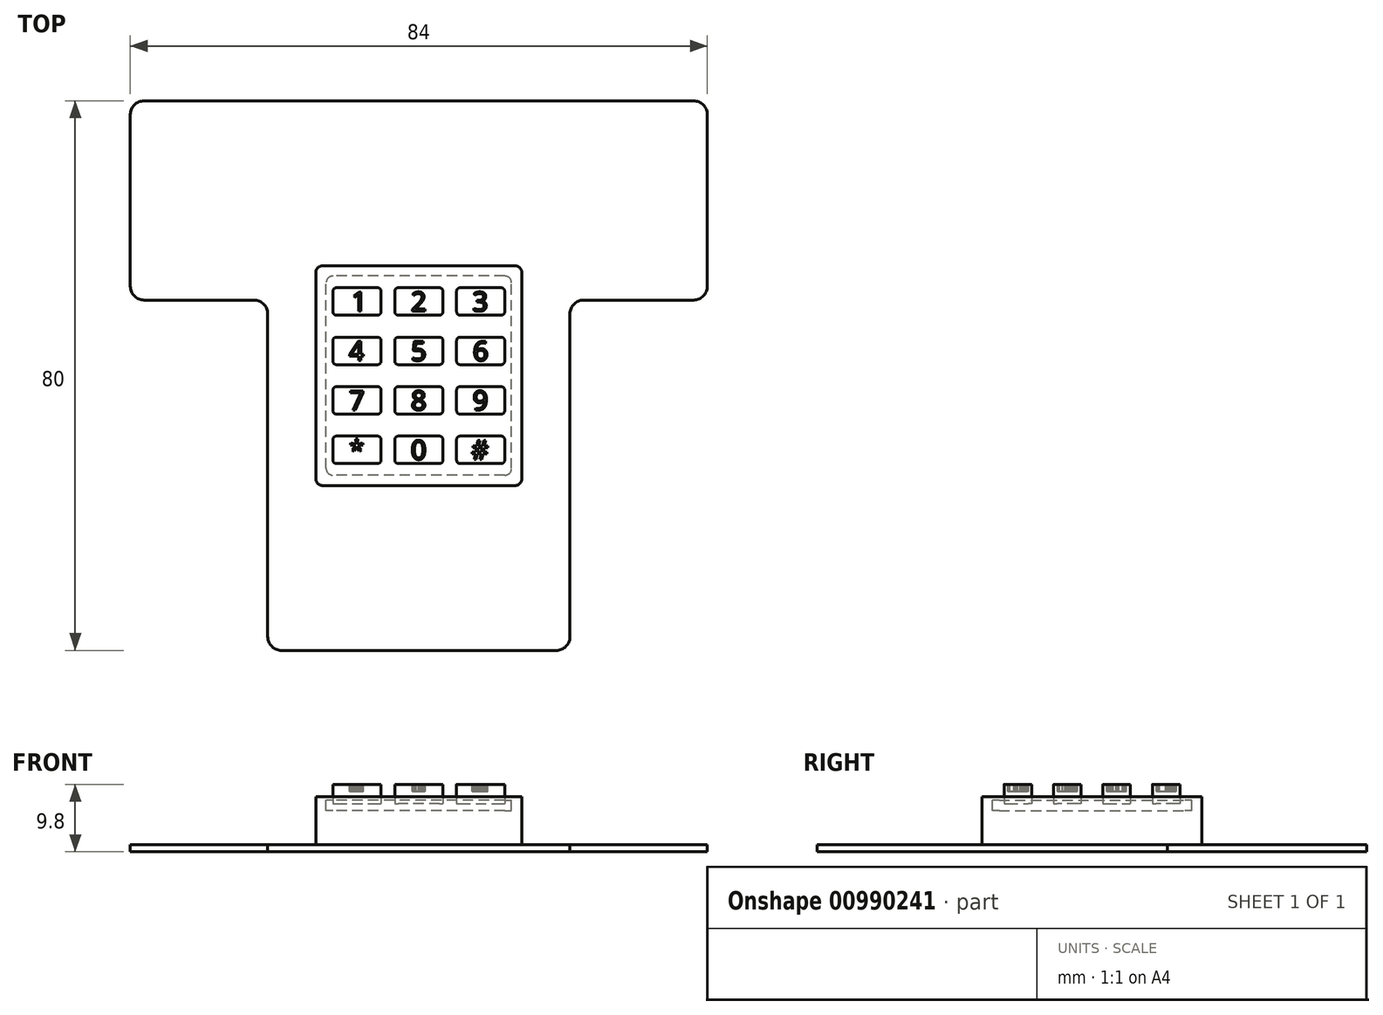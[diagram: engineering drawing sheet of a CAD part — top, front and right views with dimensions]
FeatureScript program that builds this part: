
annotation { "Feature Type Name" : "Feature", "Feature Type Description" : "" }
export const myFeature = defineFeature(function(context is Context, id is Id, definition is map)
    precondition{}
    {
        {
            var Q0;
            Q0=qCreatedBy(makeId("Top.planeOp"),FACE);
            var sketch = newSketch(context, id + "F0", { "sketchPlane" : qUnion([Q0])});
            skLineSegment(sketch, "E0.bottom", {"start": v(-15, 16) * mm, "end": v(15, 16) * mm});
            skLineSegment(sketch, "E0.top", {"start": v(-15, -16) * mm, "end": v(15, -16) * mm});
            skLineSegment(sketch, "E0.left", {"start": v(-15, 16) * mm, "end": v(-15, -16) * mm});
            skLineSegment(sketch, "E0.right", {"start": v(15, 16) * mm, "end": v(15, -16) * mm});
            skPoint(sketch, "E0.middle", {"position": v(0, 0) * mm});
            skSolve(sketch);
        }
        {
            var Q0;
            Q0 = qSketchRegion(id + "F0", true);
            extrude(context, id + "F1", {"entities" : qUnion([Q0]), "depth" : 7 * mm, "offsetDistance" : 25 * mm});
        }
        {
            var Q0;
            Q0=makeQuery(id+"F1.opExtrude","SWEPT_EDGE",EDGE,{"disambiguationData":[OSD([sQuery(id+"F0.wireOp",EDGE,"E0.bottom"),sQuery(id+"F0.wireOp",EDGE,"E0.left")])]});
            var Q1;
            Q1=makeQuery(id+"F1.opExtrude","SWEPT_EDGE",EDGE,{"disambiguationData":[OSD([sQuery(id+"F0.wireOp",EDGE,"E0.bottom"),sQuery(id+"F0.wireOp",EDGE,"E0.right")])]});
            var Q2;
            Q2=makeQuery(id+"F1.opExtrude","SWEPT_EDGE",EDGE,{"disambiguationData":[OSD([sQuery(id+"F0.wireOp",EDGE,"E0.top"),sQuery(id+"F0.wireOp",EDGE,"E0.right")])]});
            var Q3;
            Q3=makeQuery(id+"F1.opExtrude","SWEPT_EDGE",EDGE,{"disambiguationData":[OSD([sQuery(id+"F0.wireOp",EDGE,"E0.top"),sQuery(id+"F0.wireOp",EDGE,"E0.left")])]});
            fillet(context, id + "F2", {"entities" : qUnion([Q0, Q1, Q2, Q3]), "radius" : 1 * mm, "tangentPropagation" : true, "allowEdgeOverflow" : false});
        }
        {
            var Q0;
            Q0=makeQuery(id+"F1.opExtrude","CAP_FACE",FACE,{"disambiguationData":[OSD([sQuery(id+"F0.wireOp",EDGE,"E0.bottom"),sQuery(id+"F0.wireOp",EDGE,"E0.top"),sQuery(id+"F0.wireOp",EDGE,"E0.left"),sQuery(id+"F0.wireOp",EDGE,"E0.right")])],"isStart":true});
            var sketch = newSketch(context, id + "F3", { "sketchPlane" : qUnion([Q0])});
            skLineSegment(sketch, "E1.bottom", {"start": v(-22, 40) * mm, "end": v(22, 40) * mm});
            skLineSegment(sketch, "E1.top", {"start": v(-22, -40) * mm, "end": v(22, -40) * mm});
            skLineSegment(sketch, "E1.left", {"start": v(-22, 40) * mm, "end": v(-22, -40) * mm});
            skLineSegment(sketch, "E1.right", {"start": v(22, 40) * mm, "end": v(22, -40) * mm});
            skPoint(sketch, "E1.middle", {"position": v(0, 0) * mm});
            skLineSegment(sketch, "E2", {"start": v(-42, -11) * mm, "end": v(0, -11) * mm});
            skLineSegment(sketch, "E3", {"start": v(-42, -11) * mm, "end": v(-42, -40) * mm});
            skLineSegment(sketch, "E4", {"start": v(-42, -40) * mm, "end": v(-22, -40) * mm});
            skLineSegment(sketch, "E5", {"start": v(0, 0) * mm, "end": v(0, -40) * mm, "construction": true});
            skLineSegment(sketch, "E6.MirrorCS", {"start": v(42, -11) * mm, "end": v(0, -11) * mm});
            skLineSegment(sketch, "E7.MirrorCS", {"start": v(42, -11) * mm, "end": v(42, -40) * mm});
            skLineSegment(sketch, "E8.MirrorCS", {"start": v(42, -40) * mm, "end": v(22, -40) * mm});
            skSolve(sketch);
        }
        {
            var Q0;
            Q0 = qSketchRegion(id + "F3", true);
            extrude(context, id + "F4", {"entities" : qUnion([Q0]), "depth" : 1 * mm, "offsetDistance" : 25 * mm});
        }
        {
            var Q0;
            Q0=makeQuery(id+"F4.opExtrude","SWEPT_EDGE",EDGE,{"disambiguationData":[OSD([sQuery(id+"F3.wireOp",EDGE,"E1.bottom"),sQuery(id+"F3.wireOp",EDGE,"E1.left")])]});
            var Q1;
            Q1=makeQuery(id+"F4.opExtrude","SWEPT_EDGE",EDGE,{"disambiguationData":[OSD([sQuery(id+"F3.wireOp",EDGE,"E1.bottom"),sQuery(id+"F3.wireOp",EDGE,"E1.right")])]});
            var Q2;
            Q2=makeQuery(id+"F4.opExtrude","SWEPT_EDGE",EDGE,{"disambiguationData":[OSD([sQuery(id+"F3.wireOp",EDGE,"E1.top"),sQuery(id+"F3.wireOp",EDGE,"E1.right")])]});
            var Q3;
            Q3=makeQuery(id+"F4.opExtrude","SWEPT_EDGE",EDGE,{"disambiguationData":[OSD([sQuery(id+"F3.wireOp",EDGE,"E1.top"),sQuery(id+"F3.wireOp",EDGE,"E1.left")])]});
            var Q4;
            Q4=makeQuery(id+"F4.opExtrude","SWEPT_EDGE",EDGE,{"disambiguationData":[OSD([sQuery(id+"F3.wireOp",EDGE,"E2"),sQuery(id+"F3.wireOp",EDGE,"E3")])]});
            var Q5;
            Q5=makeQuery(id+"F4.opExtrude","SWEPT_EDGE",EDGE,{"disambiguationData":[OSD([sQuery(id+"F3.wireOp",EDGE,"E3"),sQuery(id+"F3.wireOp",EDGE,"E4")])]});
            var Q6;
            Q6=makeQuery(id+"F4.opExtrude","SWEPT_EDGE",EDGE,{"disambiguationData":[OSD([sQuery(id+"F3.wireOp",EDGE,"E7.MirrorCS"),sQuery(id+"F3.wireOp",EDGE,"E8.MirrorCS")])]});
            var Q7;
            Q7=makeQuery(id+"F4.opExtrude","SWEPT_EDGE",EDGE,{"disambiguationData":[OSD([sQuery(id+"F3.wireOp",EDGE,"E6.MirrorCS"),sQuery(id+"F3.wireOp",EDGE,"E7.MirrorCS")])]});
            fillet(context, id + "F5", {"entities" : qUnion([Q0, Q1, Q2, Q3, Q4, Q5, Q6, Q7]), "radius" : 2 * mm, "tangentPropagation" : true, "allowEdgeOverflow" : false});
        }
        {
            var Q0;
            Q0=makeQuery(id+"F1.opExtrude","CAP_FACE",FACE,{"disambiguationData":[OSD([sQuery(id+"F0.wireOp",EDGE,"E0.bottom"),sQuery(id+"F0.wireOp",EDGE,"E0.top"),sQuery(id+"F0.wireOp",EDGE,"E0.left"),sQuery(id+"F0.wireOp",EDGE,"E0.right")])],"isStart":false});
            var sketch = newSketch(context, id + "F6", { "sketchPlane" : qUnion([Q0])});
            skLineSegment(sketch, "E9", {"start": v(-17.09, 12.8) * mm, "end": v(-12.5, 12.8) * mm, "construction": true});
            skLineSegment(sketch, "E10.bottom", {"start": v(-12.5, 12.8) * mm, "end": v(-5.5, 12.8) * mm});
            skLineSegment(sketch, "E11", {"start": v(-4.5, 17.09) * mm, "end": v(-4.5, -16) * mm, "construction": true});
            skLineSegment(sketch, "E12.trimOffspring", {"start": v(-5.5, 12.8) * mm, "end": v(-3.5, 12.8) * mm, "construction": true});
            skLineSegment(sketch, "E13.MirrorCS", {"start": v(3.5, 12.8) * mm, "end": v(-3.5, 12.8) * mm});
            skLineSegment(sketch, "E14.trimOffspring", {"start": v(3.5, 8.8) * mm, "end": v(3.5, 6.5) * mm, "construction": true});
            skLineSegment(sketch, "E15", {"start": v(4.5, 18.24) * mm, "end": v(4.5, -18.4) * mm, "construction": true});
            skLineSegment(sketch, "E16.MirrorCS", {"start": v(5.5, 12.8) * mm, "end": v(12.5, 12.8) * mm});
            skLineSegment(sketch, "E17", {"start": v(-16.52, 7.2) * mm, "end": v(15.94, 7.2) * mm, "construction": true});
            skLineSegment(sketch, "E18.MirrorCS", {"start": v(3.5, 2.5) * mm, "end": v(3.5, 6.5) * mm});
            skLineSegment(sketch, "E19", {"start": v(-12.5, 12.8) * mm, "end": v(-12.5, 8.8) * mm});
            skLineSegment(sketch, "E20", {"start": v(-5.5, 12.8) * mm, "end": v(-5.5, 8.8) * mm});
            skLineSegment(sketch, "E21", {"start": v(-12.5, 8.8) * mm, "end": v(-5.5, 8.8) * mm});
            skLineSegment(sketch, "E22.MirrorCS", {"start": v(-3.5, 12.8) * mm, "end": v(-3.5, 8.8) * mm});
            skLineSegment(sketch, "E23.MirrorCS", {"start": v(3.5, 12.8) * mm, "end": v(3.5, 8.8) * mm});
            skLineSegment(sketch, "E24.MirrorCS", {"start": v(3.5, 8.8) * mm, "end": v(-3.5, 8.8) * mm});
            skLineSegment(sketch, "E25.MirrorCS", {"start": v(5.5, 12.8) * mm, "end": v(5.5, 8.8) * mm});
            skLineSegment(sketch, "E26.MirrorCS", {"start": v(12.5, 12.8) * mm, "end": v(12.5, 8.8) * mm});
            skLineSegment(sketch, "E27.MirrorCS", {"start": v(5.5, 8.8) * mm, "end": v(12.5, 8.8) * mm});
            skLineSegment(sketch, "E28.MirrorCS", {"start": v(-12.5, 1.6) * mm, "end": v(-5.5, 1.6) * mm});
            skLineSegment(sketch, "E29.MirrorCS", {"start": v(-12.5, 5.6) * mm, "end": v(-5.5, 5.6) * mm});
            skLineSegment(sketch, "E30.MirrorCS", {"start": v(-12.5, 1.6) * mm, "end": v(-12.5, 5.6) * mm});
            skLineSegment(sketch, "E31.MirrorCS", {"start": v(-5.5, 1.6) * mm, "end": v(-5.5, 5.6) * mm});
            skLineSegment(sketch, "E32.MirrorCS", {"start": v(3.5, 1.6) * mm, "end": v(-3.5, 1.6) * mm});
            skLineSegment(sketch, "E33.MirrorCS", {"start": v(3.5, 5.6) * mm, "end": v(-3.5, 5.6) * mm});
            skLineSegment(sketch, "E34.MirrorCS", {"start": v(-3.5, 1.6) * mm, "end": v(-3.5, 5.6) * mm});
            skLineSegment(sketch, "E35.MirrorCS", {"start": v(3.5, 1.6) * mm, "end": v(3.5, 5.6) * mm});
            skLineSegment(sketch, "E36.MirrorCS", {"start": v(5.5, 1.6) * mm, "end": v(12.5, 1.6) * mm});
            skLineSegment(sketch, "E37.MirrorCS", {"start": v(5.5, 1.6) * mm, "end": v(5.5, 5.6) * mm});
            skLineSegment(sketch, "E38.MirrorCS", {"start": v(5.5, 5.6) * mm, "end": v(12.5, 5.6) * mm});
            skLineSegment(sketch, "E39.MirrorCS", {"start": v(12.5, 1.6) * mm, "end": v(12.5, 5.6) * mm});
            skLineSegment(sketch, "E40", {"start": v(-15, 0) * mm, "end": v(15, 0) * mm, "construction": true});
            skLineSegment(sketch, "E41.MirrorCS", {"start": v(5.5, -1.6) * mm, "end": v(12.5, -1.6) * mm});
            skLineSegment(sketch, "E42.MirrorCS", {"start": v(5.5, -1.6) * mm, "end": v(5.5, -5.6) * mm});
            skLineSegment(sketch, "E43.MirrorCS", {"start": v(5.5, -5.6) * mm, "end": v(12.5, -5.6) * mm});
            skLineSegment(sketch, "E44.MirrorCS", {"start": v(12.5, -1.6) * mm, "end": v(12.5, -5.6) * mm});
            skLineSegment(sketch, "E45.MirrorCS", {"start": v(3.5, -1.6) * mm, "end": v(3.5, -5.6) * mm});
            skLineSegment(sketch, "E46.MirrorCS", {"start": v(3.5, -5.6) * mm, "end": v(-3.5, -5.6) * mm});
            skLineSegment(sketch, "E47.MirrorCS", {"start": v(-3.5, -1.6) * mm, "end": v(-3.5, -5.6) * mm});
            skLineSegment(sketch, "E48.MirrorCS", {"start": v(3.5, -1.6) * mm, "end": v(-3.5, -1.6) * mm});
            skLineSegment(sketch, "E49.MirrorCS", {"start": v(-5.5, -1.6) * mm, "end": v(-5.5, -5.6) * mm});
            skLineSegment(sketch, "E50.MirrorCS", {"start": v(-12.5, -5.6) * mm, "end": v(-5.5, -5.6) * mm});
            skLineSegment(sketch, "E51.MirrorCS", {"start": v(-12.5, -1.6) * mm, "end": v(-5.5, -1.6) * mm});
            skLineSegment(sketch, "E52", {"start": v(-15, -7.2) * mm, "end": v(15, -7.2) * mm, "construction": true});
            skLineSegment(sketch, "E53.MirrorCS", {"start": v(-12.5, -8.8) * mm, "end": v(-5.5, -8.8) * mm});
            skLineSegment(sketch, "E54.MirrorCS", {"start": v(-12.5, -12.8) * mm, "end": v(-5.5, -12.8) * mm});
            skLineSegment(sketch, "E55.MirrorCS", {"start": v(-5.5, -12.8) * mm, "end": v(-5.5, -8.8) * mm});
            skLineSegment(sketch, "E56.MirrorCS", {"start": v(3.5, -12.8) * mm, "end": v(-3.5, -12.8) * mm});
            skLineSegment(sketch, "E57.MirrorCS", {"start": v(-3.5, -12.8) * mm, "end": v(-3.5, -8.8) * mm});
            skLineSegment(sketch, "E58.MirrorCS", {"start": v(3.5, -12.8) * mm, "end": v(3.5, -8.8) * mm});
            skLineSegment(sketch, "E59.MirrorCS", {"start": v(5.5, -12.8) * mm, "end": v(12.5, -12.8) * mm});
            skLineSegment(sketch, "E60.MirrorCS", {"start": v(12.5, -12.8) * mm, "end": v(12.5, -8.8) * mm});
            skLineSegment(sketch, "E61.MirrorCS", {"start": v(5.5, -12.8) * mm, "end": v(5.5, -8.8) * mm});
            skLineSegment(sketch, "E62.MirrorCS", {"start": v(5.5, -8.8) * mm, "end": v(12.5, -8.8) * mm});
            skLineSegment(sketch, "E63", {"start": v(-3.5, -8.8) * mm, "end": v(3.5, -8.8) * mm});
            skLineSegment(sketch, "E64", {"start": v(-12.5, -1.6) * mm, "end": v(-12.5, -5.6) * mm});
            skLineSegment(sketch, "E65", {"start": v(-12.5, -8.8) * mm, "end": v(-12.5, -12.8) * mm});
            skSolve(sketch);
        }
        {
            var Q0;
            Q0 = qSketchRegion(id + "F6", true);
            extrude(context, id + "F7", {"entities" : qUnion([Q0]), "depth" : 1.8 * mm, "offsetDistance" : 25 * mm, "hasSecondDirection" : true, "secondDirectionOppositeDirection" : true, "secondDirectionDepth" : 1 * mm});
        }
        {
            var Q0;
            Q0=makeQuery(id+"F7.opExtrude","CAP_FACE",FACE,{"disambiguationData":[OSD([sQuery(id+"F6.wireOp",EDGE,"E57.MirrorCS"),sQuery(id+"F6.wireOp",EDGE,"E58.MirrorCS"),sQuery(id+"F6.wireOp",EDGE,"E56.MirrorCS"),sQuery(id+"F6.wireOp",EDGE,"E63")])],"isStart":true});
            var sketch = newSketch(context, id + "F8", { "sketchPlane" : qUnion([Q0])});
            skLineSegment(sketch, "E66.0.0", {"start": v(14, 16) * mm, "end": v(-14, 16) * mm, "construction": true});
            skArc(sketch, "E66.0.1", {"start": v(-14, 16) * mm, "mid": v(-14.7, 15.7) * mm, "end": v(-15, 15) * mm, "construction": true});
            skLineSegment(sketch, "E66.0.2", {"start": v(-15, 15) * mm, "end": v(-15, -15) * mm, "construction": true});
            skArc(sketch, "E66.0.3", {"start": v(-15, -15) * mm, "mid": v(-14.7, -15.7) * mm, "end": v(-14, -16) * mm, "construction": true});
            skLineSegment(sketch, "E66.0.4", {"start": v(-14, -16) * mm, "end": v(14, -16) * mm, "construction": true});
            skArc(sketch, "E66.0.5", {"start": v(14, -16) * mm, "mid": v(14.7, -15.7) * mm, "end": v(15, -15) * mm, "construction": true});
            skLineSegment(sketch, "E66.0.6", {"start": v(15, -15) * mm, "end": v(15, 15) * mm, "construction": true});
            skArc(sketch, "E66.0.7", {"start": v(15, 15) * mm, "mid": v(14.7, 15.7) * mm, "end": v(14, 16) * mm, "construction": true});
            skLineSegment(sketch, "E67.bottom", {"start": v(12.5, 14.5) * mm, "end": v(-12.5, 14.5) * mm});
            skLineSegment(sketch, "E67.top", {"start": v(12.5, -14.5) * mm, "end": v(-12.5, -14.5) * mm});
            skLineSegment(sketch, "E67.left", {"start": v(13.5, 13.5) * mm, "end": v(13.5, -13.5) * mm});
            skLineSegment(sketch, "E67.right", {"start": v(-13.5, 13.5) * mm, "end": v(-13.5, -13.5) * mm});
            skPoint(sketch, "E67.middle", {"position": v(0, 0) * mm});
            skPoint(sketch, "E68.visualSharp", {"position": v(13.5, 14.5) * mm});
            skArc(sketch, "E68.filletArc", {"start": v(13.5, 13.5) * mm, "mid": v(13.2, 14.2) * mm, "end": v(12.5, 14.5) * mm});
            skPoint(sketch, "E69.visualSharp", {"position": v(13.5, -14.5) * mm});
            skArc(sketch, "E69.filletArc", {"start": v(12.5, -14.5) * mm, "mid": v(13.2, -14.2) * mm, "end": v(13.5, -13.5) * mm});
            skPoint(sketch, "E70.visualSharp", {"position": v(-13.5, -14.5) * mm});
            skArc(sketch, "E70.filletArc", {"start": v(-13.5, -13.5) * mm, "mid": v(-13.2, -14.2) * mm, "end": v(-12.5, -14.5) * mm});
            skPoint(sketch, "E71.visualSharp", {"position": v(-13.5, 14.5) * mm});
            skArc(sketch, "E71.filletArc", {"start": v(-12.5, 14.5) * mm, "mid": v(-13.2, 14.2) * mm, "end": v(-13.5, 13.5) * mm});
            skSolve(sketch);
        }
        {
            var Q0;
            Q0 = qSketchRegion(id + "F8", true);
            extrude(context, id + "F9", {"entities" : qUnion([Q0]), "depth" : 1 * mm, "offsetDistance" : 25 * mm, "hasSecondDirection" : true, "secondDirectionOppositeDirection" : true, "secondDirectionDepth" : 0.5 * mm});
        }
        {
            var Q0;
            Q0=makeQuery(id+"F7.opExtrude","CAP_FACE",FACE,{"disambiguationData":[OSD([sQuery(id+"F6.wireOp",EDGE,"E10.bottom"),sQuery(id+"F6.wireOp",EDGE,"E19"),sQuery(id+"F6.wireOp",EDGE,"E20"),sQuery(id+"F6.wireOp",EDGE,"E21")])],"isStart":false});
            var sketch = newSketch(context, id + "F10", { "sketchPlane" : qUnion([Q0])});
            skLineSegment(sketch, "E72.0", {"start": v(-12.5, 12.8) * mm, "end": v(-5.5, 12.8) * mm, "construction": true});
            skLineSegment(sketch, "E72.1", {"start": v(-12.5, 8.8) * mm, "end": v(-5.5, 8.8) * mm, "construction": true});
            skLineSegment(sketch, "E72.2", {"start": v(-12.5, 5.6) * mm, "end": v(-5.5, 5.6) * mm, "construction": true});
            skLineSegment(sketch, "E72.3", {"start": v(-12.5, 1.6) * mm, "end": v(-5.5, 1.6) * mm, "construction": true});
            skLineSegment(sketch, "E72.4", {"start": v(-12.5, -1.6) * mm, "end": v(-5.5, -1.6) * mm, "construction": true});
            skLineSegment(sketch, "E72.5", {"start": v(-12.5, -5.6) * mm, "end": v(-5.5, -5.6) * mm, "construction": true});
            skLineSegment(sketch, "E72.6", {"start": v(-12.5, -8.8) * mm, "end": v(-5.5, -8.8) * mm, "construction": true});
            skLineSegment(sketch, "E72.7", {"start": v(-12.5, -12.8) * mm, "end": v(-5.5, -12.8) * mm, "construction": true});
            skLineSegment(sketch, "E73", {"start": v(-9, 12.8) * mm, "end": v(-9, -12.8) * mm, "construction": true});
            skLineSegment(sketch, "E74", {"start": v(0, 12.9) * mm, "end": v(0, -12.8) * mm, "construction": true});
            skLineSegment(sketch, "E75.MirrorCS", {"start": v(9, 12.8) * mm, "end": v(9, -12.8) * mm, "construction": true});
            skLineSegment(sketch, "E76", {"start": v(-13.4, 0) * mm, "end": v(13.4, 0) * mm, "construction": true});
            skLineSegment(sketch, "E77", {"start": v(-12.5, 12.2) * mm, "end": v(12.63, 12.2) * mm, "construction": true});
            skLineSegment(sketch, "E78", {"start": v(-12.5, 9.4) * mm, "end": v(12.28, 9.4) * mm, "construction": true});
            skLineSegment(sketch, "E79", {"start": v(-12.5, 5) * mm, "end": v(14.26, 5) * mm, "construction": true});
            skLineSegment(sketch, "E80", {"start": v(-12.47, 2.2) * mm, "end": v(14.82, 2.2) * mm, "construction": true});
            skLineSegment(sketch, "E81.MirrorCS", {"start": v(-12.47, -2.2) * mm, "end": v(14.82, -2.2) * mm, "construction": true});
            skLineSegment(sketch, "E82.MirrorCS", {"start": v(-12.5, -5) * mm, "end": v(14.26, -5) * mm, "construction": true});
            skLineSegment(sketch, "E83.MirrorCS", {"start": v(-12.5, -9.4) * mm, "end": v(12.28, -9.4) * mm, "construction": true});
            skLineSegment(sketch, "E84.MirrorCS", {"start": v(-12.5, -12.2) * mm, "end": v(12.63, -12.2) * mm, "construction": true});
            skText(sketch, "E85", { "text": "1", "fontName": "OpenSans-Regular.ttf"});
            skText(sketch, "E86", { "text": "2", "fontName": "OpenSans-Regular.ttf"});
            skText(sketch, "E87", { "text": "3", "fontName": "OpenSans-Regular.ttf"});
            skText(sketch, "E88", { "text": "4", "fontName": "OpenSans-Regular.ttf"});
            skText(sketch, "E89", { "text": "5", "fontName": "OpenSans-Regular.ttf"});
            skText(sketch, "E90", { "text": "6", "fontName": "OpenSans-Regular.ttf"});
            skText(sketch, "E91", { "text": "7", "fontName": "OpenSans-Regular.ttf"});
            skText(sketch, "E92", { "text": "8", "fontName": "OpenSans-Regular.ttf"});
            skPoint(sketch, "E92.firstSnap0", {"position": v(-1.13, 3.6) * mm});
            skText(sketch, "E93", { "text": "9", "fontName": "OpenSans-Regular.ttf"});
            skText(sketch, "E94", { "text": "0", "fontName": "OpenSans-Regular.ttf"});
            skText(sketch, "E95", { "text": "*", "fontName": "OpenSans-Regular.ttf"});
            skText(sketch, "E96", { "text": "#", "fontName": "OpenSans-Regular.ttf"});
            const initialGuessF10  = {"E85": [-0.0098, 0.0094, 1, 0, 0.0028], "E86": [-0.00113, 0.0094, 1, 0, 0.0028], "E87": [0.00783, 0.0094, 1, 0, 0.0028], "E88": [-0.0102, 0.0022, 1, 0, 0.0028], "E89": [-0.00113, 0.0022, 1, 0, 0.0028], "E90": [0.00788, 0.0022, 1, 0, 0.0028], "E91": [-0.01014, -0.005, 1, 0, 0.0028], "E92": [-0.00113, -0.005, 1, 0, 0.0028], "E93": [0.00784, -0.005, 1, 0, 0.0028], "E94": [-0.00114, -0.0122, 1, 0, 0.0028], "E95": [-0.01011, -0.0122, 1, 0, 0.0028], "E96": [0.00764, -0.0122, 1, 0, 0.0028]};
            skSetInitialGuess(sketch, initialGuessF10);
            skSolve(sketch);
        }
        {
            var Q0;
            Q0 = qSketchRegion(id + "F10", true);
            extrude(context, id + "F11", {"entities" : qUnion([Q0]), "operationType" : NewBodyOperationType.REMOVE, "oppositeDirection" : true, "depth" : 1 * mm, "offsetDistance" : 25 * mm});
        }
        {
            var Q0;
            Q0=makeQuery(id+"F7.opExtrude","SWEPT_EDGE",EDGE,{"disambiguationData":[OSD([sQuery(id+"F6.wireOp",EDGE,"E19"),sQuery(id+"F6.wireOp",EDGE,"E21")])]});
            var Q1;
            Q1=makeQuery(id+"F7.opExtrude","SWEPT_EDGE",EDGE,{"disambiguationData":[OSD([sQuery(id+"F6.wireOp",EDGE,"E28.MirrorCS"),sQuery(id+"F6.wireOp",EDGE,"E30.MirrorCS")])]});
            var Q2;
            Q2=makeQuery(id+"F7.opExtrude","SWEPT_EDGE",EDGE,{"disambiguationData":[OSD([sQuery(id+"F6.wireOp",EDGE,"E50.MirrorCS"),sQuery(id+"F6.wireOp",EDGE,"E64")])]});
            var Q3;
            Q3=makeQuery(id+"F7.opExtrude","SWEPT_EDGE",EDGE,{"disambiguationData":[OSD([sQuery(id+"F6.wireOp",EDGE,"E54.MirrorCS"),sQuery(id+"F6.wireOp",EDGE,"E65")])]});
            var Q4;
            Q4=makeQuery(id+"F7.opExtrude","SWEPT_EDGE",EDGE,{"disambiguationData":[OSD([sQuery(id+"F6.wireOp",EDGE,"E57.MirrorCS"),sQuery(id+"F6.wireOp",EDGE,"E56.MirrorCS")])]});
            var Q5;
            Q5=makeQuery(id+"F7.opExtrude","SWEPT_EDGE",EDGE,{"disambiguationData":[OSD([sQuery(id+"F6.wireOp",EDGE,"E46.MirrorCS"),sQuery(id+"F6.wireOp",EDGE,"E47.MirrorCS")])]});
            var Q6;
            Q6=makeQuery(id+"F7.opExtrude","SWEPT_EDGE",EDGE,{"disambiguationData":[OSD([sQuery(id+"F6.wireOp",EDGE,"E32.MirrorCS"),sQuery(id+"F6.wireOp",EDGE,"E34.MirrorCS")])]});
            var Q7;
            Q7=makeQuery(id+"F7.opExtrude","SWEPT_EDGE",EDGE,{"disambiguationData":[OSD([sQuery(id+"F6.wireOp",EDGE,"E22.MirrorCS"),sQuery(id+"F6.wireOp",EDGE,"E24.MirrorCS")])]});
            var Q8;
            Q8=makeQuery(id+"F7.opExtrude","SWEPT_EDGE",EDGE,{"disambiguationData":[OSD([sQuery(id+"F6.wireOp",EDGE,"E25.MirrorCS"),sQuery(id+"F6.wireOp",EDGE,"E27.MirrorCS")])]});
            var Q9;
            Q9=makeQuery(id+"F7.opExtrude","SWEPT_EDGE",EDGE,{"disambiguationData":[OSD([sQuery(id+"F6.wireOp",EDGE,"E36.MirrorCS"),sQuery(id+"F6.wireOp",EDGE,"E37.MirrorCS")])]});
            var Q10;
            Q10=makeQuery(id+"F7.opExtrude","SWEPT_EDGE",EDGE,{"disambiguationData":[OSD([sQuery(id+"F6.wireOp",EDGE,"E42.MirrorCS"),sQuery(id+"F6.wireOp",EDGE,"E43.MirrorCS")])]});
            var Q11;
            Q11=makeQuery(id+"F7.opExtrude","SWEPT_EDGE",EDGE,{"disambiguationData":[OSD([sQuery(id+"F6.wireOp",EDGE,"E59.MirrorCS"),sQuery(id+"F6.wireOp",EDGE,"E61.MirrorCS")])]});
            var Q12;
            Q12=makeQuery(id+"F7.opExtrude","SWEPT_EDGE",EDGE,{"disambiguationData":[OSD([sQuery(id+"F6.wireOp",EDGE,"E10.bottom"),sQuery(id+"F6.wireOp",EDGE,"E19")])]});
            var Q13;
            Q13=makeQuery(id+"F7.opExtrude","SWEPT_EDGE",EDGE,{"disambiguationData":[OSD([sQuery(id+"F6.wireOp",EDGE,"E29.MirrorCS"),sQuery(id+"F6.wireOp",EDGE,"E30.MirrorCS")])]});
            var Q14;
            Q14=makeQuery(id+"F7.opExtrude","SWEPT_EDGE",EDGE,{"disambiguationData":[OSD([sQuery(id+"F6.wireOp",EDGE,"E51.MirrorCS"),sQuery(id+"F6.wireOp",EDGE,"E64")])]});
            var Q15;
            Q15=makeQuery(id+"F7.opExtrude","SWEPT_EDGE",EDGE,{"disambiguationData":[OSD([sQuery(id+"F6.wireOp",EDGE,"E53.MirrorCS"),sQuery(id+"F6.wireOp",EDGE,"E65")])]});
            var Q16;
            Q16=makeQuery(id+"F7.opExtrude","SWEPT_EDGE",EDGE,{"disambiguationData":[OSD([sQuery(id+"F6.wireOp",EDGE,"E57.MirrorCS"),sQuery(id+"F6.wireOp",EDGE,"E63")])]});
            var Q17;
            Q17=makeQuery(id+"F7.opExtrude","SWEPT_EDGE",EDGE,{"disambiguationData":[OSD([sQuery(id+"F6.wireOp",EDGE,"E47.MirrorCS"),sQuery(id+"F6.wireOp",EDGE,"E48.MirrorCS")])]});
            var Q18;
            Q18=makeQuery(id+"F7.opExtrude","SWEPT_EDGE",EDGE,{"disambiguationData":[OSD([sQuery(id+"F6.wireOp",EDGE,"E33.MirrorCS"),sQuery(id+"F6.wireOp",EDGE,"E34.MirrorCS")])]});
            var Q19;
            Q19=makeQuery(id+"F7.opExtrude","SWEPT_EDGE",EDGE,{"disambiguationData":[OSD([sQuery(id+"F6.wireOp",EDGE,"E13.MirrorCS"),sQuery(id+"F6.wireOp",EDGE,"E22.MirrorCS")])]});
            var Q20;
            Q20=makeQuery(id+"F7.opExtrude","SWEPT_EDGE",EDGE,{"disambiguationData":[OSD([sQuery(id+"F6.wireOp",EDGE,"E16.MirrorCS"),sQuery(id+"F6.wireOp",EDGE,"E25.MirrorCS")])]});
            var Q21;
            Q21=makeQuery(id+"F7.opExtrude","SWEPT_EDGE",EDGE,{"disambiguationData":[OSD([sQuery(id+"F6.wireOp",EDGE,"E37.MirrorCS"),sQuery(id+"F6.wireOp",EDGE,"E38.MirrorCS")])]});
            var Q22;
            Q22=makeQuery(id+"F7.opExtrude","SWEPT_EDGE",EDGE,{"disambiguationData":[OSD([sQuery(id+"F6.wireOp",EDGE,"E41.MirrorCS"),sQuery(id+"F6.wireOp",EDGE,"E42.MirrorCS")])]});
            var Q23;
            Q23=makeQuery(id+"F7.opExtrude","SWEPT_EDGE",EDGE,{"disambiguationData":[OSD([sQuery(id+"F6.wireOp",EDGE,"E61.MirrorCS"),sQuery(id+"F6.wireOp",EDGE,"E62.MirrorCS")])]});
            var Q24;
            Q24=makeQuery(id+"F7.opExtrude","SWEPT_EDGE",EDGE,{"disambiguationData":[OSD([sQuery(id+"F6.wireOp",EDGE,"E16.MirrorCS"),sQuery(id+"F6.wireOp",EDGE,"E26.MirrorCS")])]});
            var Q25;
            Q25=makeQuery(id+"F7.opExtrude","SWEPT_EDGE",EDGE,{"disambiguationData":[OSD([sQuery(id+"F6.wireOp",EDGE,"E13.MirrorCS"),sQuery(id+"F6.wireOp",EDGE,"E23.MirrorCS")])]});
            var Q26;
            Q26=makeQuery(id+"F7.opExtrude","SWEPT_EDGE",EDGE,{"disambiguationData":[OSD([sQuery(id+"F6.wireOp",EDGE,"E10.bottom"),sQuery(id+"F6.wireOp",EDGE,"E20")])]});
            var Q27;
            Q27=makeQuery(id+"F7.opExtrude","SWEPT_EDGE",EDGE,{"disambiguationData":[OSD([sQuery(id+"F6.wireOp",EDGE,"E29.MirrorCS"),sQuery(id+"F6.wireOp",EDGE,"E31.MirrorCS")])]});
            var Q28;
            Q28=makeQuery(id+"F7.opExtrude","SWEPT_EDGE",EDGE,{"disambiguationData":[OSD([sQuery(id+"F6.wireOp",EDGE,"E33.MirrorCS"),sQuery(id+"F6.wireOp",EDGE,"E35.MirrorCS")])]});
            var Q29;
            Q29=makeQuery(id+"F7.opExtrude","SWEPT_EDGE",EDGE,{"disambiguationData":[OSD([sQuery(id+"F6.wireOp",EDGE,"E38.MirrorCS"),sQuery(id+"F6.wireOp",EDGE,"E39.MirrorCS")])]});
            var Q30;
            Q30=makeQuery(id+"F7.opExtrude","SWEPT_EDGE",EDGE,{"disambiguationData":[OSD([sQuery(id+"F6.wireOp",EDGE,"E41.MirrorCS"),sQuery(id+"F6.wireOp",EDGE,"E44.MirrorCS")])]});
            var Q31;
            Q31=makeQuery(id+"F7.opExtrude","SWEPT_EDGE",EDGE,{"disambiguationData":[OSD([sQuery(id+"F6.wireOp",EDGE,"E45.MirrorCS"),sQuery(id+"F6.wireOp",EDGE,"E48.MirrorCS")])]});
            var Q32;
            Q32=makeQuery(id+"F7.opExtrude","SWEPT_EDGE",EDGE,{"disambiguationData":[OSD([sQuery(id+"F6.wireOp",EDGE,"E49.MirrorCS"),sQuery(id+"F6.wireOp",EDGE,"E51.MirrorCS")])]});
            var Q33;
            Q33=makeQuery(id+"F7.opExtrude","SWEPT_EDGE",EDGE,{"disambiguationData":[OSD([sQuery(id+"F6.wireOp",EDGE,"E60.MirrorCS"),sQuery(id+"F6.wireOp",EDGE,"E62.MirrorCS")])]});
            var Q34;
            Q34=makeQuery(id+"F7.opExtrude","SWEPT_EDGE",EDGE,{"disambiguationData":[OSD([sQuery(id+"F6.wireOp",EDGE,"E58.MirrorCS"),sQuery(id+"F6.wireOp",EDGE,"E63")])]});
            var Q35;
            Q35=makeQuery(id+"F7.opExtrude","SWEPT_EDGE",EDGE,{"disambiguationData":[OSD([sQuery(id+"F6.wireOp",EDGE,"E53.MirrorCS"),sQuery(id+"F6.wireOp",EDGE,"E55.MirrorCS")])]});
            var Q36;
            Q36=makeQuery(id+"F7.opExtrude","SWEPT_EDGE",EDGE,{"disambiguationData":[OSD([sQuery(id+"F6.wireOp",EDGE,"E59.MirrorCS"),sQuery(id+"F6.wireOp",EDGE,"E60.MirrorCS")])]});
            var Q37;
            Q37=makeQuery(id+"F7.opExtrude","SWEPT_EDGE",EDGE,{"disambiguationData":[OSD([sQuery(id+"F6.wireOp",EDGE,"E58.MirrorCS"),sQuery(id+"F6.wireOp",EDGE,"E56.MirrorCS")])]});
            var Q38;
            Q38=makeQuery(id+"F7.opExtrude","SWEPT_EDGE",EDGE,{"disambiguationData":[OSD([sQuery(id+"F6.wireOp",EDGE,"E54.MirrorCS"),sQuery(id+"F6.wireOp",EDGE,"E55.MirrorCS")])]});
            var Q39;
            Q39=makeQuery(id+"F7.opExtrude","SWEPT_EDGE",EDGE,{"disambiguationData":[OSD([sQuery(id+"F6.wireOp",EDGE,"E43.MirrorCS"),sQuery(id+"F6.wireOp",EDGE,"E44.MirrorCS")])]});
            var Q40;
            Q40=makeQuery(id+"F7.opExtrude","SWEPT_EDGE",EDGE,{"disambiguationData":[OSD([sQuery(id+"F6.wireOp",EDGE,"E45.MirrorCS"),sQuery(id+"F6.wireOp",EDGE,"E46.MirrorCS")])]});
            var Q41;
            Q41=makeQuery(id+"F7.opExtrude","SWEPT_EDGE",EDGE,{"disambiguationData":[OSD([sQuery(id+"F6.wireOp",EDGE,"E49.MirrorCS"),sQuery(id+"F6.wireOp",EDGE,"E50.MirrorCS")])]});
            var Q42;
            Q42=makeQuery(id+"F7.opExtrude","SWEPT_EDGE",EDGE,{"disambiguationData":[OSD([sQuery(id+"F6.wireOp",EDGE,"E28.MirrorCS"),sQuery(id+"F6.wireOp",EDGE,"E31.MirrorCS")])]});
            var Q43;
            Q43=makeQuery(id+"F7.opExtrude","SWEPT_EDGE",EDGE,{"disambiguationData":[OSD([sQuery(id+"F6.wireOp",EDGE,"E32.MirrorCS"),sQuery(id+"F6.wireOp",EDGE,"E35.MirrorCS")])]});
            var Q44;
            Q44=makeQuery(id+"F7.opExtrude","SWEPT_EDGE",EDGE,{"disambiguationData":[OSD([sQuery(id+"F6.wireOp",EDGE,"E36.MirrorCS"),sQuery(id+"F6.wireOp",EDGE,"E39.MirrorCS")])]});
            var Q45;
            Q45=makeQuery(id+"F7.opExtrude","SWEPT_EDGE",EDGE,{"disambiguationData":[OSD([sQuery(id+"F6.wireOp",EDGE,"E26.MirrorCS"),sQuery(id+"F6.wireOp",EDGE,"E27.MirrorCS")])]});
            var Q46;
            Q46=makeQuery(id+"F7.opExtrude","SWEPT_EDGE",EDGE,{"disambiguationData":[OSD([sQuery(id+"F6.wireOp",EDGE,"E23.MirrorCS"),sQuery(id+"F6.wireOp",EDGE,"E24.MirrorCS")])]});
            var Q47;
            Q47=makeQuery(id+"F7.opExtrude","SWEPT_EDGE",EDGE,{"disambiguationData":[OSD([sQuery(id+"F6.wireOp",EDGE,"E20"),sQuery(id+"F6.wireOp",EDGE,"E21")])]});
            fillet(context, id + "F12", {"entities" : qUnion([Q0, Q1, Q2, Q3, Q4, Q5, Q6, Q7, Q8, Q9, Q10, Q11, Q12, Q13, Q14, Q15, Q16, Q17, Q18, Q19, Q20, Q21, Q22, Q23, Q24, Q25, Q26, Q27, Q28, Q29, Q30, Q31, Q32, Q33, Q34, Q35, Q36, Q37, Q38, Q39, Q40, Q41, Q42, Q43, Q44, Q45, Q46, Q47]), "radius" : 0.5 * mm, "tangentPropagation" : true, "allowEdgeOverflow" : false});
        }
    });
